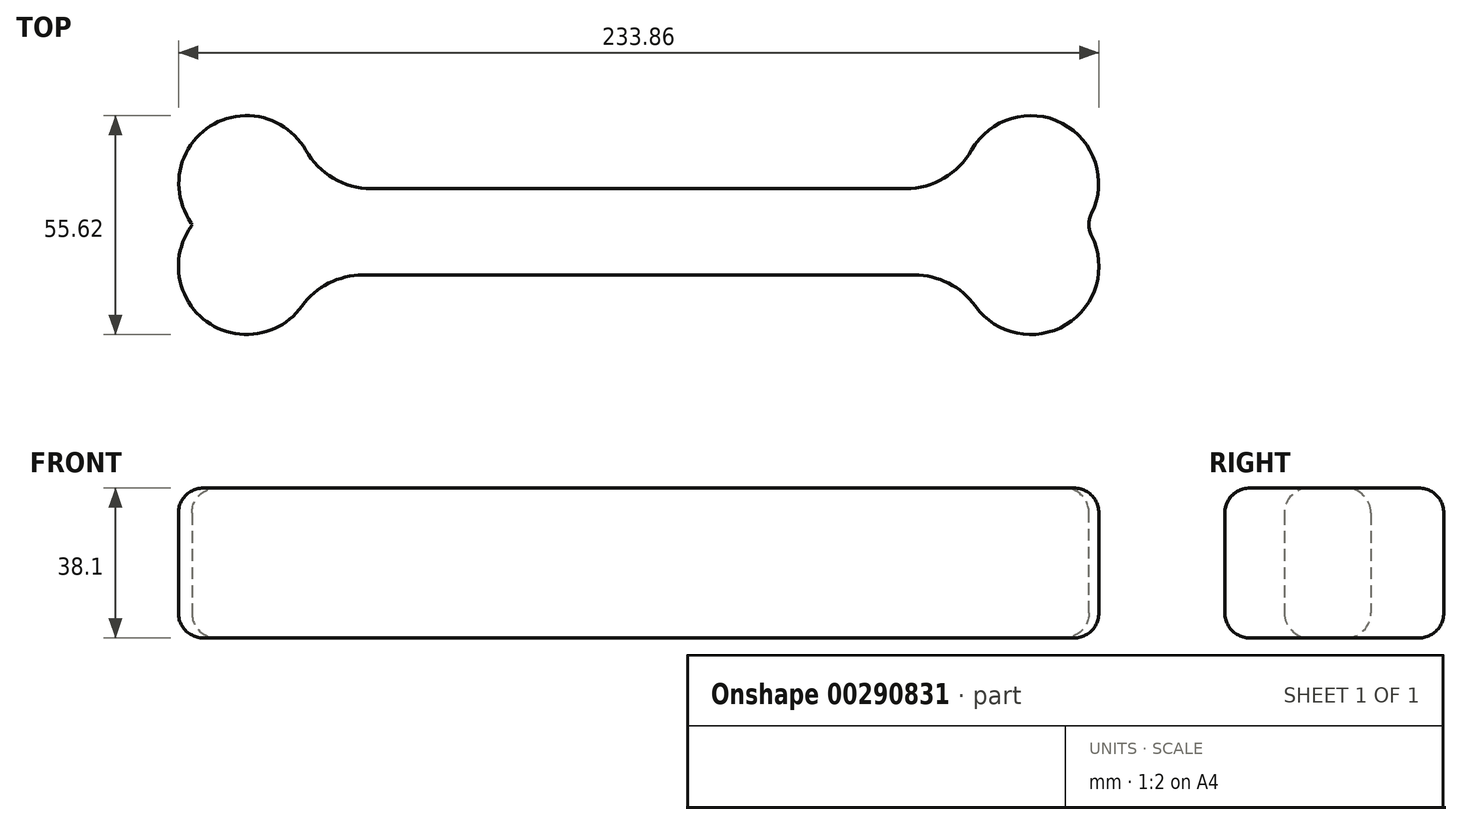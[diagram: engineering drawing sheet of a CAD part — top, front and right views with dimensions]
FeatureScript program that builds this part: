
annotation { "Feature Type Name" : "Feature", "Feature Type Description" : "" }
export const myFeature = defineFeature(function(context is Context, id is Id, definition is map)
    precondition{}
    {
        {
            var Q0;
            Q0=qCreatedBy(makeId("Top.planeOp"),FACE);
            var sketch = newSketch(context, id + "F0", { "sketchPlane" : qUnion([Q0])});
            skLineSegment(sketch, "E0", {"start": v(0, 7.2) * mm, "end": v(22.65, 7.2) * mm});
            skArc(sketch, "E1", {"start": v(33.1, 13.36) * mm, "mid": v(30.26, 12.56) * mm, "end": v(28.19, 10.43) * mm});
            skArc(sketch, "E2", {"start": v(37.77, 4.14) * mm, "mid": v(38.33, 10.21) * mm, "end": v(33.1, 13.36) * mm});
            skArc(sketch, "E3", {"start": v(33.1, -5.17) * mm, "mid": v(38.37, -1.98) * mm, "end": v(37.77, 4.14) * mm});
            skArc(sketch, "E4", {"start": v(28.51, -2.77) * mm, "mid": v(30.52, -4.52) * mm, "end": v(33.1, -5.17) * mm});
            skLineSegment(sketch, "E5", {"start": v(23.36, -0.14) * mm, "end": v(0, -0.14) * mm});
            skLineSegment(sketch, "E6.MirrorCS", {"start": v(0, 7.2) * mm, "end": v(-22.65, 7.2) * mm});
            skArc(sketch, "E7.MirrorCS", {"start": v(-33.1, 13.36) * mm, "mid": v(-30.26, 12.56) * mm, "end": v(-28.19, 10.43) * mm});
            skArc(sketch, "E8.MirrorCS", {"start": v(-37.88, 4.29) * mm, "mid": v(-38.29, 10.3) * mm, "end": v(-33.1, 13.36) * mm});
            skArc(sketch, "E9.MirrorCS", {"start": v(-33.1, -5.17) * mm, "mid": v(-38.32, -2.07) * mm, "end": v(-37.88, 3.99) * mm});
            skArc(sketch, "E10.MirrorCS", {"start": v(-28.51, -2.77) * mm, "mid": v(-30.52, -4.52) * mm, "end": v(-33.1, -5.17) * mm});
            skLineSegment(sketch, "E11.MirrorCS", {"start": v(-23.36, -0.14) * mm, "end": v(0, -0.14) * mm});
            skPoint(sketch, "E12.visualSharp", {"position": v(-27.47, 7.2) * mm});
            skArc(sketch, "E12.filletArc", {"start": v(-28.19, 10.43) * mm, "mid": v(-25.86, 8.06) * mm, "end": v(-22.65, 7.2) * mm});
            skPoint(sketch, "E13.visualSharp", {"position": v(-27.47, -0.14) * mm});
            skArc(sketch, "E13.filletArc", {"start": v(-23.36, -0.14) * mm, "mid": v(-26.25, -0.83) * mm, "end": v(-28.51, -2.77) * mm});
            skPoint(sketch, "E14.visualSharp", {"position": v(27.47, -0.14) * mm});
            skArc(sketch, "E14.filletArc", {"start": v(28.51, -2.77) * mm, "mid": v(26.25, -0.83) * mm, "end": v(23.36, -0.14) * mm});
            skPoint(sketch, "E15.visualSharp", {"position": v(27.47, 7.2) * mm});
            skArc(sketch, "E15.filletArc", {"start": v(22.65, 7.2) * mm, "mid": v(25.86, 8.06) * mm, "end": v(28.19, 10.43) * mm});
            skPoint(sketch, "E16.visualSharp", {"position": v(-37.77, 4.14) * mm});
            skArc(sketch, "E16.filletArc", {"start": v(-37.88, 3.99) * mm, "mid": v(-37.83, 4.14) * mm, "end": v(-37.88, 4.29) * mm});
            skSolve(sketch);
        }
        {
            var Q0;
            Q0=makeQuery(id+"F0.imprint","IMPRINT",FACE,{"disambiguationData":[TD([[makeQuery(id+"F0.imprint","IMPRINT",EDGE,{"derivedFrom":sQuery(id+"F0.wireOp",EDGE,"E0")}),-1.0]])]});
            extrude(context, id + "F1", {"entities" : qUnion([Q0]), "depth" : 12.7 * mm});
        }
        {
            var Q0;
            Q0=makeQuery(id+"F1.opExtrude","SWEPT_BODY",BODY,{"disambiguationData":[OSD([sQuery(id+"F0.wireOp",EDGE,"E0"),sQuery(id+"F0.wireOp",EDGE,"E1"),sQuery(id+"F0.wireOp",EDGE,"E2"),sQuery(id+"F0.wireOp",EDGE,"E3"),sQuery(id+"F0.wireOp",EDGE,"E4"),sQuery(id+"F0.wireOp",EDGE,"E5"),sQuery(id+"F0.wireOp",EDGE,"E6.MirrorCS"),sQuery(id+"F0.wireOp",EDGE,"E7.MirrorCS"),sQuery(id+"F0.wireOp",EDGE,"E8.MirrorCS"),sQuery(id+"F0.wireOp",EDGE,"E9.MirrorCS"),sQuery(id+"F0.wireOp",EDGE,"E10.MirrorCS"),sQuery(id+"F0.wireOp",EDGE,"E11.MirrorCS")])]});
            var Q1;
            Q1=qCreatedBy(makeId("Origin.pointOp"),VERTEX);
            transform(context, id + "F2", {"entities" : qUnion([Q0]), "transformType" : TransformType.SCALE_UNIFORMLY, "scale" : 3, "scalePoint" : qUnion([Q1]), "makeCopy" : false});
        }
        {
            var Q0;
            Q0=makeQuery(id+"F1.opExtrude","CAP_FACE",FACE,{"disambiguationData":[OSD([sQuery(id+"F0.wireOp",EDGE,"E0"),sQuery(id+"F0.wireOp",EDGE,"E1"),sQuery(id+"F0.wireOp",EDGE,"E2"),sQuery(id+"F0.wireOp",EDGE,"E3"),sQuery(id+"F0.wireOp",EDGE,"E4"),sQuery(id+"F0.wireOp",EDGE,"E5"),sQuery(id+"F0.wireOp",EDGE,"E6.MirrorCS"),sQuery(id+"F0.wireOp",EDGE,"E7.MirrorCS"),sQuery(id+"F0.wireOp",EDGE,"E8.MirrorCS"),sQuery(id+"F0.wireOp",EDGE,"E9.MirrorCS"),sQuery(id+"F0.wireOp",EDGE,"E10.MirrorCS"),sQuery(id+"F0.wireOp",EDGE,"E11.MirrorCS"),sQuery(id+"F0.wireOp",EDGE,"E12.filletArc"),sQuery(id+"F0.wireOp",EDGE,"E13.filletArc"),sQuery(id+"F0.wireOp",EDGE,"E14.filletArc"),sQuery(id+"F0.wireOp",EDGE,"E15.filletArc"),sQuery(id+"F0.wireOp",EDGE,"E16.filletArc")])],"isStart":false});
            var Q1;
            Q1=makeQuery(id+"F1.opExtrude","CAP_FACE",FACE,{"disambiguationData":[OSD([sQuery(id+"F0.wireOp",EDGE,"E0"),sQuery(id+"F0.wireOp",EDGE,"E1"),sQuery(id+"F0.wireOp",EDGE,"E2"),sQuery(id+"F0.wireOp",EDGE,"E3"),sQuery(id+"F0.wireOp",EDGE,"E4"),sQuery(id+"F0.wireOp",EDGE,"E5"),sQuery(id+"F0.wireOp",EDGE,"E6.MirrorCS"),sQuery(id+"F0.wireOp",EDGE,"E7.MirrorCS"),sQuery(id+"F0.wireOp",EDGE,"E8.MirrorCS"),sQuery(id+"F0.wireOp",EDGE,"E9.MirrorCS"),sQuery(id+"F0.wireOp",EDGE,"E10.MirrorCS"),sQuery(id+"F0.wireOp",EDGE,"E11.MirrorCS"),sQuery(id+"F0.wireOp",EDGE,"E12.filletArc"),sQuery(id+"F0.wireOp",EDGE,"E13.filletArc"),sQuery(id+"F0.wireOp",EDGE,"E14.filletArc"),sQuery(id+"F0.wireOp",EDGE,"E15.filletArc"),sQuery(id+"F0.wireOp",EDGE,"E16.filletArc")])],"isStart":true});
            var Q2;
            Q2=makeQuery(id+"F1.opExtrude","SWEPT_EDGE",EDGE,{"disambiguationData":[OSD([sQuery(id+"F0.wireOp",EDGE,"E2"),sQuery(id+"F0.wireOp",EDGE,"E3")])]});
            fillet(context, id + "F3", {"entities" : qUnion([Q0, Q1, Q2]), "radius" : 6.35 * mm, "tangentPropagation" : true, "allowEdgeOverflow" : false});
        }
    });
